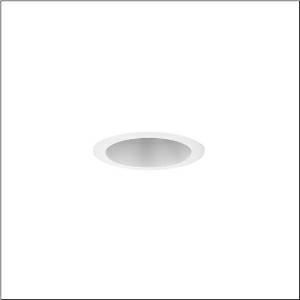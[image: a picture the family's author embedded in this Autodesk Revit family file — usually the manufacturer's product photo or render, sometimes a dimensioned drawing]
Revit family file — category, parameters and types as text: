
# Revit family: lunis_31-l_51dn15ee31b
name_source: partatom
category: Lighting Fixtures
units: mm (PartAtom-declared; Revit-internal decimal feet)

## family parameters
Cut with Voids When Loaded = No
Host = Face
Light Source = No
Part Type = Normal
Room Calculation Point = No
Round Connector Dimension = Use Diameter
Shared = No

## types (1)
- --- (1 x LED, 1650 lm, 12.2 W, 3000K)
    Apparent Load = 12 VA
    CIE Flux Codes = 93 98 100 100 100
    Color Rendering = 80
    Color Temperature = 3000K
    Default Elevation = 1800 mm
    Description = Lunis 31-L, downlight, light control with reflector, light emission: direct distribution, LED rated luminous flux: 1.650lm, light colour: 830, mains connection: 220..240V, AC/DC, 0/50..60Hz, housing, of aluminium, white, protection rating (complete): IP20, protection rating (on room side): IP54, insulation class (complete): insulation class II (safety insulation), certification: CE, ENEC, packaging unit: 1 piece
    Height = 0 mm  [stored 0 ft]
    Lamp = 1 x LED
    Lamp Light Flux = 1650 lm
    Lamp Power = 12.2 W
    Lamp count = 1
    Length = 188 mm  [stored 0.616798 ft]
    Luminous efficacy = 135 lm/W
    Manufacturer = Siteco
    ModVariant = No
    Model = 51DN15EE31B
    Mounting Place = Ceiling
    Mounting Type = Recessed
    Number of Poles = 1
    OnlyDefault = Yes
    Power Factor = 1
    Product Name = Lunis 31-L
    Product group = downlight
    ProductGroupID = 401
    Protection Class = Protection class II
    Protection Degree = IP 20
    RLX_Detail_Level = 1
    RLX_Emergency_Light_Flux = 0 lm
    RLX_Emergency_Type = 0
    RLX_Emergency_Type_DB = No
    RlxData = <blob elided: 22217 chars, md5=8611c185>
    Socket = socket
    Standby Power = 0 W
    System Light Flux = 1650 lm
    System Power = 12 W
    Type Comments = individual setting: luminous flux: 100 % | (OFF | ON) | 300 mA
    Type Image = l_1345911.jpg
    URL = http://relux.com
    VarID = @adj_029669
    Voltage = 0 V
    Weight = 0.00 kg
    Width = 0 mm  [stored 0 ft]

note: [stored X ft] marks values corroborated as IEEE doubles in the binary element streams (Revit-internal decimal feet)

## geometry (parser evidence)
native form markers: Blend x4, Sweep x10
no freeform markers — native parametric forms only
